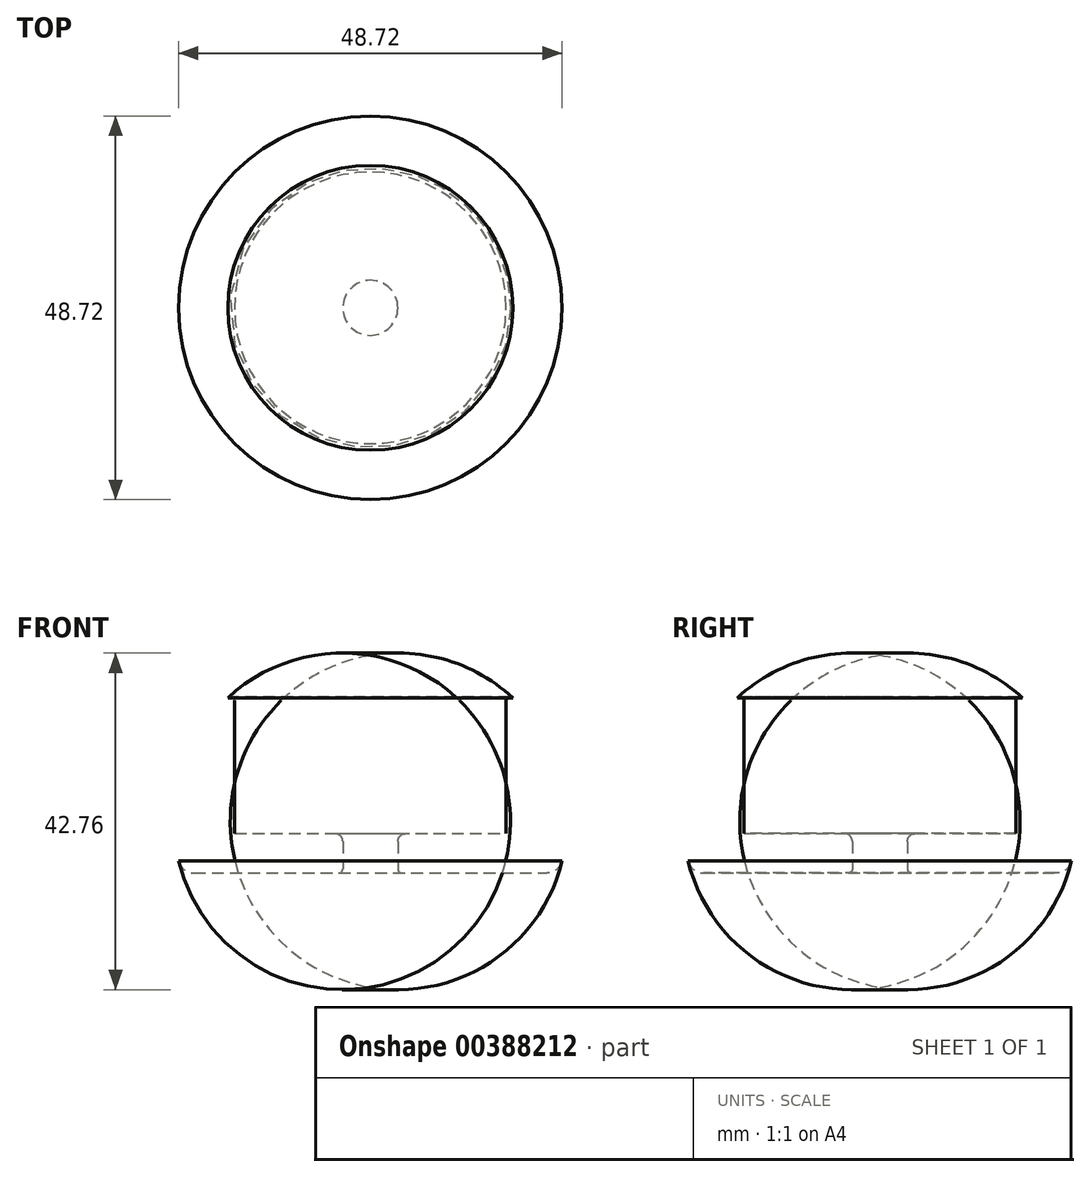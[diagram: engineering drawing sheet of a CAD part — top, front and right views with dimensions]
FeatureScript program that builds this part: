
annotation { "Feature Type Name" : "Feature", "Feature Type Description" : "" }
export const myFeature = defineFeature(function(context is Context, id is Id, definition is map)
    precondition{}
    {
        {
            var Q0;
            Q0=qCreatedBy(makeId("Front.planeOp"),FACE);
            var sketch = newSketch(context, id + "F0", { "sketchPlane" : qUnion([Q0])});
            skLineSegment(sketch, "E0", {"start": v(0, 0) * mm, "end": v(0, 23) * mm});
            skLineSegment(sketch, "E1", {"start": v(0, 0) * mm, "end": v(3.5, 0) * mm});
            skLineSegment(sketch, "E2", {"start": v(4, 0) * mm, "end": v(22.41, 0) * mm});
            skLineSegment(sketch, "E3", {"start": v(3.5, 0.5) * mm, "end": v(3.5, 4) * mm});
            skLineSegment(sketch, "E4", {"start": v(0, 23) * mm, "end": v(17.25, 23) * mm});
            skArc(sketch, "E5", {"start": v(24.36, 1.53) * mm, "mid": v(24.05, 12.75) * mm, "end": v(18.1, 22.26) * mm});
            skLineSegment(sketch, "E6", {"start": v(17.25, 21.9) * mm, "end": v(17.25, 5) * mm});
            skLineSegment(sketch, "E7", {"start": v(4.5, 5) * mm, "end": v(17.25, 5) * mm});
            skPoint(sketch, "E8.visualSharp", {"position": v(3.5, 5) * mm});
            skArc(sketch, "E8.filletArc", {"start": v(4.5, 5) * mm, "mid": v(3.8, 4.7) * mm, "end": v(3.5, 4) * mm});
            skPoint(sketch, "E9.visualSharp", {"position": v(3.5, 0) * mm});
            skArc(sketch, "E9.filletArc", {"start": v(3.5, 0.5) * mm, "mid": v(3.65, 0.15) * mm, "end": v(4, 0) * mm});
            skPoint(sketch, "E10.visualSharp", {"position": v(17.25, 23) * mm});
            skArc(sketch, "E10.filletArc", {"start": v(18.1, 22.26) * mm, "mid": v(17.55, 22.35) * mm, "end": v(17.25, 21.9) * mm});
            skPoint(sketch, "E11.visualSharp", {"position": v(23.93, 0) * mm});
            skArc(sketch, "E11.filletArc", {"start": v(22.41, 0) * mm, "mid": v(23.65, 0.43) * mm, "end": v(24.36, 1.53) * mm});
            skSolve(sketch);
        }
        {
            var Q0;
            Q0=makeQuery(id+"F0.imprint","IMPRINT",FACE,{"disambiguationData":[TD([[makeQuery(id+"F0.imprint","IMPRINT",EDGE,{"derivedFrom":sQuery(id+"F0.wireOp",EDGE,"E2")}),1.0]])]});
            var Q1;
            Q1=sQuery(id+"F0.wireOp",EDGE,"E0");
            revolve(context, id + "F1", {"entities" : qUnion([Q0]), "axis" : qUnion([Q1]), "revolveType" : RevolveType.FULL});
        }
    });
